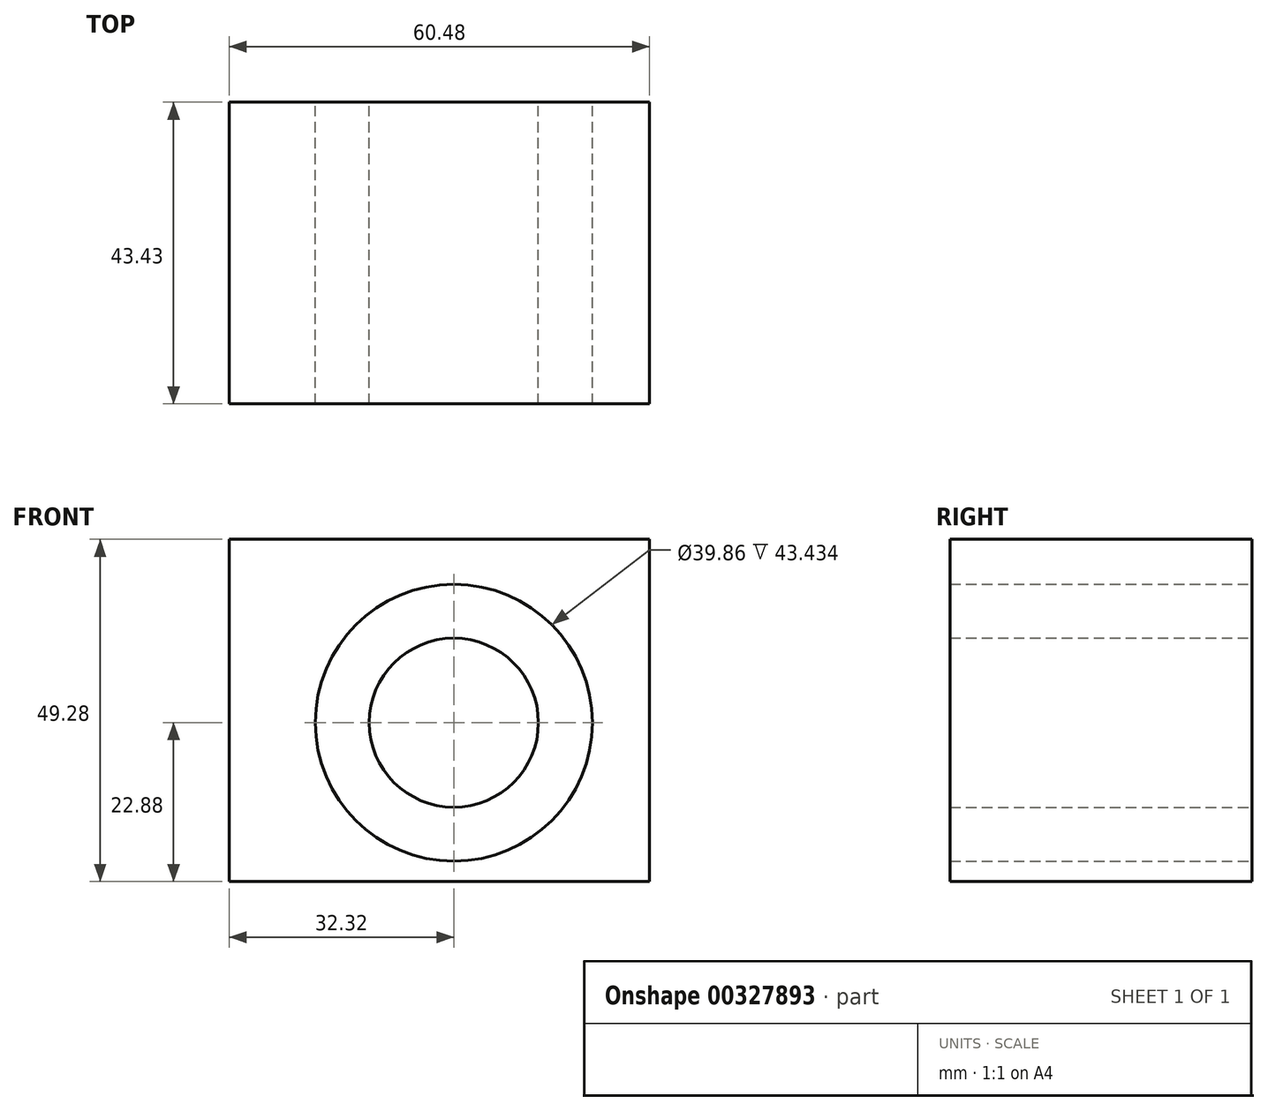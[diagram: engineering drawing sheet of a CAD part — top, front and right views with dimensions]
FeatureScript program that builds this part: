
annotation { "Feature Type Name" : "Feature", "Feature Type Description" : "" }
export const myFeature = defineFeature(function(context is Context, id is Id, definition is map)
    precondition{}
    {
        {
            var Q0;
            Q0=qCreatedBy(makeId("Front.planeOp"),FACE);
            var sketch = newSketch(context, id + "F0", { "sketchPlane" : qUnion([Q0])});
            skLineSegment(sketch, "E0.bottom", {"start": v(-32.32, 26.4) * mm, "end": v(28.16, 26.4) * mm});
            skLineSegment(sketch, "E0.top", {"start": v(-32.32, -22.88) * mm, "end": v(28.16, -22.88) * mm});
            skLineSegment(sketch, "E0.left", {"start": v(-32.32, 26.4) * mm, "end": v(-32.32, -22.88) * mm});
            skLineSegment(sketch, "E0.right", {"start": v(28.16, 26.4) * mm, "end": v(28.16, -22.88) * mm});
            skCircle(sketch, "E1", {"center": v(0, 0) * mm, "radius": 12.17 * mm});
            skCircle(sketch, "E2", {"center": v(0, 0) * mm, "radius": 19.93 * mm});
            skSolve(sketch);
        }
        {
            var Q0;
            Q0=makeQuery(id+"F0.imprint","IMPRINT",FACE,{"disambiguationData":[TD([[makeQuery(id+"F0.imprint","IMPRINT",EDGE,{"derivedFrom":sQuery(id+"F0.wireOp",EDGE,"E0.bottom")}),-1.0]])]});
            var Q1;
            Q1=makeQuery(id+"F0.imprint","IMPRINT",FACE,{"disambiguationData":[TD([[makeQuery(id+"F0.imprint","IMPRINT",EDGE,{"derivedFrom":sQuery(id+"F0.wireOp",EDGE,"E1")}),1.0]])]});
            extrude(context, id + "F1", {"entities" : qUnion([Q0, Q1]), "depth" : 43.43 * mm});
        }
        {
            var Q0;
            Q0=qCreatedBy(makeId("Front.planeOp"),FACE);
            var sketch = newSketch(context, id + "F2", { "sketchPlane" : qUnion([Q0])});
            skText(sketch, "E3", { "text": "Hello Juggy", "fontName": "OpenSans-Bold.ttf"});
            const initialGuessF2  = {"E3": [-0.02413, 0.02025, 1, 0, 0.00583]};
            skSetInitialGuess(sketch, initialGuessF2);
            skSolve(sketch);
        }
        {
            var Q0;
            Q0 = qSketchRegion(id + "F2", true);
            var Q1;
            Q1 = qConstructionFilter(qBodyType(qCreatedBy(id + "F2" ,EDGE), BodyType.WIRE), ConstructionObject.NO);
            extrude(context, id + "F3", {"entities" : qUnion([Q0]), "bodyType" : ToolBodyType.SURFACE, "operationType" : NewBodyOperationType.REMOVE, "surfaceEntities" : qUnion([Q1]), "depth" : 2.54 * mm});
        }
    });
